# Revit family: for update_48001AUS_NEWWWW
name_source: partatom
category: Plumbing Fixtures
revit_build: Autodesk Revit 2018 (Build: 20170223_1515(x64)
units: mm (PartAtom-declared; Revit-internal decimal feet)

## family parameters
Always vertical = No
Cut with Voids When Loaded = No
OmniClass Number = 23.31.11.00
OmniClass Title = Faucets
Part Type = Normal
Room Calculation Point = No
Round Connector Dimension = Use Diameter
Shared = No
Work Plane-Based = Yes

## types (3) — shared parameters
Always visible = Yes
BIMobject category = Taps & Mixers
Connector Description = Water Inlet 12.7mm
Date of publishing = 9/28/2022 12:00:00 AM
Default Elevation = 1219.2 mm  [stored 4 ft]
Description = AXOR One Single lever basin mixer 70 with lever handle without waste set
Design country = Germany
Diameter = 13 mm
EAN code = 4059625381342
Edition number = 1
GTIN code = https://4059625381342
IFC Classification = Valve
Manufacturer = AXOR
Manufacturer country = Germany
Manufacturer name = AXOR
Masterformat 2014 Code = 22 41 39
Masterformat 2014 Description = Residential Faucets, Supplies, and Trim
Model = 48001AUS
OmniClass Code = 23-31 11 00
OmniClass Description = Faucets
Product Guid = ea1a8f37-0d6f-4b7c-be53-a18ae5f001bb
Product SKU = 48001AUS
Product data url = https://bimobject.com
Product family = AXOR One
Product group = Basin mixers
Product name = 48001AUS AXOR One Single lever basin mixer 70 with lever handle without waste set
Product url = https://www.axor-design.com
QR code = https://bimobject.com
UNSPSC Code = 301815
URL = https://www.axor-design.com
Uniclass 2015 Code = Pr_40_20_87
Uniclass 2015 Name = Taps and water supply outlet fittings
Uniformat II Code = D2010
Uniformat II Description = Plumbing Fixtures
Weight Net (Kg) = 1

## per-type parameters (varying)
| type | Material 1 |
| 703 Matte White | AXOR - Metal - 703 Matte White |
| 673 Matte Black | AXOR - Metal - 673 Matte Black |
| 003 Chrome | AXOR - Metal - 003 Chrome |

note: [stored X ft] marks values corroborated as IEEE doubles in the binary element streams (Revit-internal decimal feet)

## geometry (parser evidence)
native form markers: Sweep x1
no freeform markers — native parametric forms only
